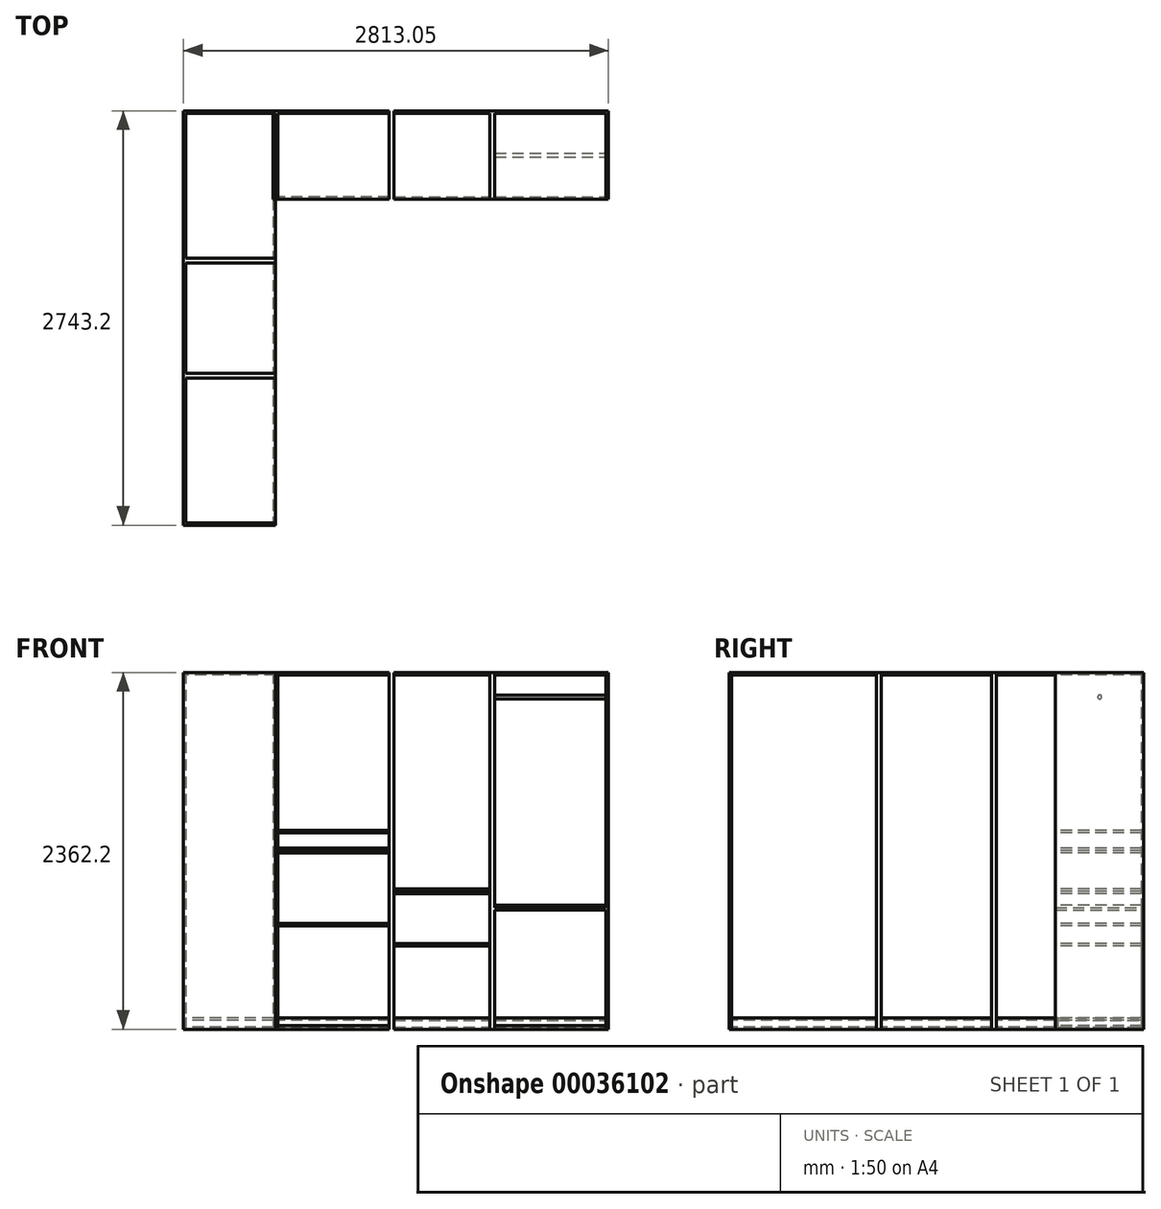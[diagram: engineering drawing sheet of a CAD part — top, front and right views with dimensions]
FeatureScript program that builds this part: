
annotation { "Feature Type Name" : "Feature", "Feature Type Description" : "" }
export const myFeature = defineFeature(function(context is Context, id is Id, definition is map)
    precondition{}
    {
        {
            var Q0;
            Q0=qCreatedBy(makeId("Top.planeOp"),FACE);
            var sketch = newSketch(context, id + "F0", { "sketchPlane" : qUnion([Q0])});
            skLineSegment(sketch, "E0.rect.bottom", {"start": v(384.18, 292.1) * mm, "end": v(-384.18, 292.1) * mm});
            skLineSegment(sketch, "E0.rect.top", {"start": v(384.18, -292.1) * mm, "end": v(-384.18, -292.1) * mm});
            skLineSegment(sketch, "E0.rect.left", {"start": v(384.18, 292.1) * mm, "end": v(384.18, -292.1) * mm});
            skLineSegment(sketch, "E0.rect.right", {"start": v(-384.18, 292.1) * mm, "end": v(-384.18, -292.1) * mm});
            skPoint(sketch, "E0.rect.middle", {"position": v(0, 0) * mm});
            skLineSegment(sketch, "E1.bottom", {"start": v(384.18, -292.1) * mm, "end": v(1050.93, -292.1) * mm});
            skLineSegment(sketch, "E1.top", {"start": v(384.17, 292.1) * mm, "end": v(1050.92, 292.1) * mm});
            skLineSegment(sketch, "E1.left", {"start": v(384.18, -292.1) * mm, "end": v(384.18, 292.1) * mm});
            skLineSegment(sketch, "E1.right", {"start": v(1050.93, -292.1) * mm, "end": v(1050.92, 292.1) * mm});
            skLineSegment(sketch, "E2.bottom", {"start": v(1050.93, -292.1) * mm, "end": v(1819.27, -292.1) * mm});
            skLineSegment(sketch, "E2.top", {"start": v(1050.92, 292.1) * mm, "end": v(1819.27, 292.1) * mm});
            skLineSegment(sketch, "E2.left", {"start": v(1050.93, -292.1) * mm, "end": v(1050.93, 292.1) * mm});
            skLineSegment(sketch, "E2.right", {"start": v(1819.27, -292.1) * mm, "end": v(1819.27, 292.1) * mm});
            skLineSegment(sketch, "E3.bottom", {"start": v(-384.18, 292.1) * mm, "end": v(-993.78, 292.1) * mm});
            skLineSegment(sketch, "E3.top", {"start": v(-384.17, -2451.1) * mm, "end": v(-993.77, -2451.1) * mm});
            skLineSegment(sketch, "E3.left", {"start": v(-384.18, 292.1) * mm, "end": v(-384.18, -2451.1) * mm});
            skLineSegment(sketch, "E3.right", {"start": v(-993.78, 292.1) * mm, "end": v(-993.77, -2451.1) * mm});
            skLineSegment(sketch, "E4.0", {"start": v(1066.8, -276.22) * mm, "end": v(1066.8, 276.22) * mm});
            skLineSegment(sketch, "E4.1", {"start": v(1066.8, -276.22) * mm, "end": v(1803.4, -276.22) * mm});
            skLineSegment(sketch, "E4.2", {"start": v(1803.4, -276.22) * mm, "end": v(1803.4, 276.22) * mm});
            skLineSegment(sketch, "E4.3", {"start": v(1066.8, 276.22) * mm, "end": v(1803.4, 276.22) * mm});
            skLineSegment(sketch, "E5.0", {"start": v(400.05, -276.23) * mm, "end": v(1035.05, -276.23) * mm});
            skLineSegment(sketch, "E5.1", {"start": v(400.05, -276.23) * mm, "end": v(400.05, 276.23) * mm});
            skLineSegment(sketch, "E5.2", {"start": v(400.05, 276.23) * mm, "end": v(1035.05, 276.23) * mm});
            skLineSegment(sketch, "E5.3", {"start": v(1035.05, -276.23) * mm, "end": v(1035.05, 276.23) * mm});
            skLineSegment(sketch, "E6.0", {"start": v(368.3, -276.23) * mm, "end": v(-368.3, -276.23) * mm});
            skLineSegment(sketch, "E6.1", {"start": v(368.3, -276.23) * mm, "end": v(368.3, 276.22) * mm});
            skLineSegment(sketch, "E6.2", {"start": v(368.3, 276.22) * mm, "end": v(-368.3, 276.22) * mm});
            skLineSegment(sketch, "E6.3", {"start": v(-368.3, 276.22) * mm, "end": v(-368.3, -276.23) * mm});
            skLineSegment(sketch, "E7.0", {"start": v(-400.05, 276.22) * mm, "end": v(-977.9, 276.22) * mm});
            skLineSegment(sketch, "E7.1", {"start": v(-400.05, 276.22) * mm, "end": v(-400.05, -682.63) * mm});
            skLineSegment(sketch, "E7.2", {"start": v(-400.05, -2435.23) * mm, "end": v(-977.9, -2435.23) * mm});
            skLineSegment(sketch, "E7.3", {"start": v(-977.9, 276.22) * mm, "end": v(-977.9, -682.63) * mm});
            skLineSegment(sketch, "E8", {"start": v(-368.3, 276.22) * mm, "end": v(-368.3, 292.1) * mm});
            skLineSegment(sketch, "E9", {"start": v(-368.3, -276.23) * mm, "end": v(-368.3, -292.1) * mm});
            skLineSegment(sketch, "E10", {"start": v(-400.05, 276.22) * mm, "end": v(-384.18, 276.22) * mm});
            skLineSegment(sketch, "E11", {"start": v(368.3, -276.23) * mm, "end": v(368.3, -292.1) * mm});
            skLineSegment(sketch, "E12", {"start": v(368.3, 276.22) * mm, "end": v(368.3, 292.1) * mm});
            skLineSegment(sketch, "E13", {"start": v(400.05, -276.23) * mm, "end": v(400.05, -292.1) * mm});
            skLineSegment(sketch, "E14", {"start": v(400.05, 276.23) * mm, "end": v(400.05, 292.1) * mm});
            skLineSegment(sketch, "E15", {"start": v(1035.05, 276.23) * mm, "end": v(1035.05, 292.1) * mm});
            skLineSegment(sketch, "E16", {"start": v(1066.8, 276.22) * mm, "end": v(1066.8, 292.1) * mm});
            skLineSegment(sketch, "E17", {"start": v(1035.05, -276.23) * mm, "end": v(1035.05, -292.1) * mm});
            skLineSegment(sketch, "E18", {"start": v(1066.8, -276.22) * mm, "end": v(1066.8, -292.1) * mm});
            skLineSegment(sketch, "E19", {"start": v(1803.4, 276.22) * mm, "end": v(1803.4, 292.1) * mm});
            skLineSegment(sketch, "E20", {"start": v(1803.4, -276.22) * mm, "end": v(1803.4, -292.1) * mm});
            skLineSegment(sketch, "E21", {"start": v(-977.9, 276.22) * mm, "end": v(-993.78, 276.22) * mm});
            skLineSegment(sketch, "E22.0", {"start": v(-384.18, -698.5) * mm, "end": v(-993.77, -698.5) * mm});
            skLineSegment(sketch, "E23", {"start": v(-977.9, -2435.23) * mm, "end": v(-993.77, -2435.23) * mm});
            skLineSegment(sketch, "E24", {"start": v(-400.05, -2435.23) * mm, "end": v(-384.18, -2435.23) * mm});
            skLineSegment(sketch, "E25.0", {"start": v(-384.17, -1460.5) * mm, "end": v(-993.77, -1460.5) * mm});
            skLineSegment(sketch, "E26.0", {"start": v(-384.18, -714.38) * mm, "end": v(-993.77, -714.38) * mm});
            skLineSegment(sketch, "E27.0", {"start": v(-384.18, -682.63) * mm, "end": v(-993.77, -682.63) * mm});
            skLineSegment(sketch, "E28.0", {"start": v(-384.17, -1444.62) * mm, "end": v(-993.77, -1444.62) * mm});
            skLineSegment(sketch, "E29.0", {"start": v(-384.17, -1476.38) * mm, "end": v(-993.77, -1476.38) * mm});
            skLineSegment(sketch, "E30.trimOffspring", {"start": v(-977.9, -714.38) * mm, "end": v(-977.9, -1444.62) * mm});
            skLineSegment(sketch, "E31.trimOffspring", {"start": v(-400.05, -714.38) * mm, "end": v(-400.05, -1444.62) * mm});
            skLineSegment(sketch, "E32.trimOffspring", {"start": v(-977.9, -1476.38) * mm, "end": v(-977.9, -2435.23) * mm});
            skLineSegment(sketch, "E33.trimOffspring", {"start": v(-400.05, -1476.38) * mm, "end": v(-400.05, -2435.23) * mm});
            skLineSegment(sketch, "E34", {"start": v(-384.18, -292.1) * mm, "end": v(-400.05, -292.1) * mm});
            skLineSegment(sketch, "E35.bottom", {"start": v(-384.17, -2451.1) * mm, "end": v(384.18, -2451.1) * mm});
            skLineSegment(sketch, "E35.top", {"start": v(-384.17, -1866.9) * mm, "end": v(384.18, -1866.9) * mm});
            skLineSegment(sketch, "E35.left", {"start": v(-384.17, -2451.1) * mm, "end": v(-384.17, -1866.9) * mm});
            skLineSegment(sketch, "E35.right", {"start": v(384.18, -2451.1) * mm, "end": v(384.18, -1866.9) * mm});
            skLineSegment(sketch, "E36", {"start": v(-384.17, -1866.9) * mm, "end": v(-400.05, -1866.9) * mm});
            skSolve(sketch);
        }
        {
            var Q0;
            {var subQ2=sQuery(id+"F0.wireOp",EDGE,"E30.trimOffspring");Q0=makeQuery(id+"F0.imprint","IMPRINT",FACE,{"disambiguationData":[TD([[makeQuery(id+"F0.imprint","IMPRINT",EDGE,{"derivedFrom":subQ2}),1.0]])]});}
            var Q1;
            Q1=makeQuery(id+"F0.imprint","IMPRINT",FACE,{"disambiguationData":[TD([[makeQuery(id+"F0.imprint","IMPRINT",EDGE,{"derivedFrom":sQuery(id+"F0.wireOp",EDGE,"E7.2")}),-1.0]])]});
            var Q2;
            {var subQ5=sQuery(id+"F0.wireOp",EDGE,"E7.0");Q2=makeQuery(id+"F0.imprint","IMPRINT",FACE,{"disambiguationData":[TD([[makeQuery(id+"F0.imprint","IMPRINT",EDGE,{"derivedFrom":subQ5}),1.0]])]});}
            var Q3;
            Q3=makeQuery(id+"F0.imprint","IMPRINT",FACE,{"disambiguationData":[TD([[makeQuery(id+"F0.imprint","IMPRINT",EDGE,{"derivedFrom":sQuery(id+"F0.wireOp",EDGE,"E6.0")}),-1.0]])]});
            var Q4;
            Q4=makeQuery(id+"F0.imprint","IMPRINT",FACE,{"disambiguationData":[TD([[makeQuery(id+"F0.imprint","IMPRINT",EDGE,{"derivedFrom":sQuery(id+"F0.wireOp",EDGE,"E5.0")}),1.0]])]});
            var Q5;
            Q5=makeQuery(id+"F0.imprint","IMPRINT",FACE,{"disambiguationData":[TD([[makeQuery(id+"F0.imprint","IMPRINT",EDGE,{"derivedFrom":sQuery(id+"F0.wireOp",EDGE,"E4.0")}),-1.0]])]});
            extrude(context, id + "F1", {"entities" : qUnion([Q0, Q1, Q2, Q3, Q4, Q5]), "depth" : 15.88 * mm});
        }
        {
            var Q0;
            {var subQ3=sQuery(id+"F0.wireOp",EDGE,"E3.top");Q0=makeQuery(id+"F0.imprint","IMPRINT",FACE,{"disambiguationData":[TD([[makeQuery(id+"F0.imprint","IMPRINT",EDGE,{"derivedFrom":subQ3}),-1.0]])]});}
            var Q1;
            {var subQ4=sQuery(id+"F0.wireOp",EDGE,"E23");Q1=makeQuery(id+"F0.imprint","IMPRINT",FACE,{"disambiguationData":[TD([[makeQuery(id+"F0.imprint","IMPRINT",EDGE,{"derivedFrom":subQ4}),-1.0]])]});}
            var Q2;
            {var subQ7=sQuery(id+"F0.wireOp",EDGE,"E25.0");Q2=makeQuery(id+"F0.imprint","IMPRINT",FACE,{"disambiguationData":[TD([[makeQuery(id+"F0.imprint","IMPRINT",EDGE,{"derivedFrom":subQ7}),1.0]])]});}
            var Q3;
            {var subQ7=sQuery(id+"F0.wireOp",EDGE,"E25.0");Q3=makeQuery(id+"F0.imprint","IMPRINT",FACE,{"disambiguationData":[TD([[makeQuery(id+"F0.imprint","IMPRINT",EDGE,{"derivedFrom":subQ7}),-1.0]])]});}
            var Q4;
            {var subQ1=sQuery(id+"F0.wireOp",EDGE,"E30.trimOffspring");Q4=makeQuery(id+"F0.imprint","IMPRINT",FACE,{"disambiguationData":[TD([[makeQuery(id+"F0.imprint","IMPRINT",EDGE,{"derivedFrom":subQ1}),-1.0]])]});}
            var Q5;
            {var subQ5=sQuery(id+"F0.wireOp",EDGE,"E22.0");Q5=makeQuery(id+"F0.imprint","IMPRINT",FACE,{"disambiguationData":[TD([[makeQuery(id+"F0.imprint","IMPRINT",EDGE,{"derivedFrom":subQ5}),1.0]])]});}
            var Q6;
            {var subQ7=sQuery(id+"F0.wireOp",EDGE,"E22.0");Q6=makeQuery(id+"F0.imprint","IMPRINT",FACE,{"disambiguationData":[TD([[makeQuery(id+"F0.imprint","IMPRINT",EDGE,{"derivedFrom":subQ7}),-1.0]])]});}
            var Q7;
            {var subQ1=sQuery(id+"F0.wireOp",EDGE,"E10");Q7=makeQuery(id+"F0.imprint","IMPRINT",FACE,{"disambiguationData":[TD([[makeQuery(id+"F0.imprint","IMPRINT",EDGE,{"derivedFrom":subQ1}),-1.0]])]});}
            var Q8;
            Q8=makeQuery(id+"F0.imprint","IMPRINT",FACE,{"disambiguationData":[TD([[makeQuery(id+"F0.imprint","IMPRINT",EDGE,{"derivedFrom":sQuery(id+"F0.wireOp",EDGE,"E6.3")}),-1.0]])]});
            var Q9;
            {var subQ3=sQuery(id+"F0.wireOp",EDGE,"E7.3");Q9=makeQuery(id+"F0.imprint","IMPRINT",FACE,{"disambiguationData":[TD([[makeQuery(id+"F0.imprint","IMPRINT",EDGE,{"derivedFrom":subQ3}),-1.0]])]});}
            var Q10;
            {var subQ3=sQuery(id+"F0.wireOp",EDGE,"E3.bottom");Q10=makeQuery(id+"F0.imprint","IMPRINT",FACE,{"disambiguationData":[TD([[makeQuery(id+"F0.imprint","IMPRINT",EDGE,{"derivedFrom":subQ3}),1.0]])]});}
            var Q11;
            Q11=makeQuery(id+"F0.imprint","IMPRINT",FACE,{"disambiguationData":[TD([[makeQuery(id+"F0.imprint","IMPRINT",EDGE,{"derivedFrom":sQuery(id+"F0.wireOp",EDGE,"E6.2")}),-1.0]])]});
            var Q12;
            {var subQ2=sQuery(id+"F0.wireOp",EDGE,"E1.left");Q12=makeQuery(id+"F0.imprint","IMPRINT",FACE,{"disambiguationData":[TD([[makeQuery(id+"F0.imprint","IMPRINT",EDGE,{"derivedFrom":subQ2}),1.0]])]});}
            var Q13;
            {var subQ1=sQuery(id+"F0.wireOp",EDGE,"E1.left");Q13=makeQuery(id+"F0.imprint","IMPRINT",FACE,{"disambiguationData":[TD([[makeQuery(id+"F0.imprint","IMPRINT",EDGE,{"derivedFrom":subQ1}),-1.0]])]});}
            var Q14;
            Q14=makeQuery(id+"F0.imprint","IMPRINT",FACE,{"disambiguationData":[TD([[makeQuery(id+"F0.imprint","IMPRINT",EDGE,{"derivedFrom":sQuery(id+"F0.wireOp",EDGE,"E5.2")}),1.0]])]});
            var Q15;
            {var subQ1=sQuery(id+"F0.wireOp",EDGE,"E2.left");Q15=makeQuery(id+"F0.imprint","IMPRINT",FACE,{"disambiguationData":[TD([[makeQuery(id+"F0.imprint","IMPRINT",EDGE,{"derivedFrom":subQ1}),1.0]])]});}
            var Q16;
            {var subQ2=sQuery(id+"F0.wireOp",EDGE,"E2.left");Q16=makeQuery(id+"F0.imprint","IMPRINT",FACE,{"disambiguationData":[TD([[makeQuery(id+"F0.imprint","IMPRINT",EDGE,{"derivedFrom":subQ2}),-1.0]])]});}
            var Q17;
            Q17=makeQuery(id+"F0.imprint","IMPRINT",FACE,{"disambiguationData":[TD([[makeQuery(id+"F0.imprint","IMPRINT",EDGE,{"derivedFrom":sQuery(id+"F0.wireOp",EDGE,"E4.3")}),1.0]])]});
            var Q18;
            {var subQ2=sQuery(id+"F0.wireOp",EDGE,"E2.right");Q18=makeQuery(id+"F0.imprint","IMPRINT",FACE,{"disambiguationData":[TD([[makeQuery(id+"F0.imprint","IMPRINT",EDGE,{"derivedFrom":subQ2}),1.0]])]});}
            extrude(context, id + "F2", {"entities" : qUnion([Q0, Q1, Q2, Q3, Q4, Q5, Q6, Q7, Q8, Q9, Q10, Q11, Q12, Q13, Q14, Q15, Q16, Q17, Q18]), "depth" : 2362.2 * mm});
        }
        {
            var Q0;
            {var subQ2=sQuery(id+"F0.wireOp",EDGE,"E24");Q0=makeQuery(id+"F0.imprint","IMPRINT",FACE,{"disambiguationData":[TD([[makeQuery(id+"F0.imprint","IMPRINT",EDGE,{"derivedFrom":subQ2}),1.0]])]});}
            var Q1;
            {var subQ0=sQuery(id+"F0.wireOp",EDGE,"E36");Q1=makeQuery(id+"F0.imprint","IMPRINT",FACE,{"disambiguationData":[TD([[makeQuery(id+"F0.imprint","IMPRINT",EDGE,{"derivedFrom":subQ0}),-1.0]])]});}
            var Q2;
            {var subQ0=sQuery(id+"F0.wireOp",EDGE,"E31.trimOffspring");Q2=makeQuery(id+"F0.imprint","IMPRINT",FACE,{"disambiguationData":[TD([[makeQuery(id+"F0.imprint","IMPRINT",EDGE,{"derivedFrom":subQ0}),1.0]])]});}
            var Q3;
            {var subQ0=sQuery(id+"F0.wireOp",EDGE,"E34");Q3=makeQuery(id+"F0.imprint","IMPRINT",FACE,{"disambiguationData":[TD([[makeQuery(id+"F0.imprint","IMPRINT",EDGE,{"derivedFrom":subQ0}),1.0]])]});}
            var Q4;
            Q4=makeQuery(id+"F0.imprint","IMPRINT",FACE,{"disambiguationData":[TD([[makeQuery(id+"F0.imprint","IMPRINT",EDGE,{"derivedFrom":sQuery(id+"F0.wireOp",EDGE,"E6.0")}),1.0]])]});
            var Q5;
            Q5=makeQuery(id+"F0.imprint","IMPRINT",FACE,{"disambiguationData":[TD([[makeQuery(id+"F0.imprint","IMPRINT",EDGE,{"derivedFrom":sQuery(id+"F0.wireOp",EDGE,"E5.0")}),-1.0]])]});
            var Q6;
            Q6=makeQuery(id+"F0.imprint","IMPRINT",FACE,{"disambiguationData":[TD([[makeQuery(id+"F0.imprint","IMPRINT",EDGE,{"derivedFrom":sQuery(id+"F0.wireOp",EDGE,"E4.1")}),-1.0]])]});
            extrude(context, id + "F3", {"entities" : qUnion([Q0, Q1, Q2, Q3, Q4, Q5, Q6]), "depth" : 76.2 * mm});
        }
        {
            var Q0;
            {var subQ2=sQuery(id+"F0.wireOp",EDGE,"E7.2");Q0=makeQuery(id+"F0.imprint","IMPRINT",FACE,{"disambiguationData":[TD([[makeQuery(id+"F0.imprint","IMPRINT",EDGE,{"derivedFrom":subQ2}),-1.0]])]});}
            var Q1;
            {var subQ2=sQuery(id+"F0.wireOp",EDGE,"E30.trimOffspring");Q1=makeQuery(id+"F0.imprint","IMPRINT",FACE,{"disambiguationData":[TD([[makeQuery(id+"F0.imprint","IMPRINT",EDGE,{"derivedFrom":subQ2}),1.0]])]});}
            var Q2;
            {var subQ5=sQuery(id+"F0.wireOp",EDGE,"E7.0");Q2=makeQuery(id+"F0.imprint","IMPRINT",FACE,{"disambiguationData":[TD([[makeQuery(id+"F0.imprint","IMPRINT",EDGE,{"derivedFrom":subQ5}),1.0]])]});}
            var Q3;
            Q3=makeQuery(id+"F0.imprint","IMPRINT",FACE,{"disambiguationData":[TD([[makeQuery(id+"F0.imprint","IMPRINT",EDGE,{"derivedFrom":sQuery(id+"F0.wireOp",EDGE,"E6.0")}),-1.0]])]});
            var Q4;
            Q4=makeQuery(id+"F0.imprint","IMPRINT",FACE,{"disambiguationData":[TD([[makeQuery(id+"F0.imprint","IMPRINT",EDGE,{"derivedFrom":sQuery(id+"F0.wireOp",EDGE,"E5.0")}),1.0]])]});
            var Q5;
            Q5=makeQuery(id+"F0.imprint","IMPRINT",FACE,{"disambiguationData":[TD([[makeQuery(id+"F0.imprint","IMPRINT",EDGE,{"derivedFrom":sQuery(id+"F0.wireOp",EDGE,"E4.0")}),-1.0]])]});
            extrude(context, id + "F4", {"entities" : qUnion([Q0, Q1, Q2, Q3, Q4, Q5]), "depth" : 76.2 * mm, "hasSecondDirection" : true, "secondDirectionOppositeDirection" : false, "secondDirectionDepth" : 60.32 * mm});
        }
        {
            var Q0;
            {var subQ2=sQuery(id+"F0.wireOp",EDGE,"E24");Q0=makeQuery(id+"F0.imprint","IMPRINT",FACE,{"disambiguationData":[TD([[makeQuery(id+"F0.imprint","IMPRINT",EDGE,{"derivedFrom":subQ2}),1.0]])]});}
            var Q1;
            {var subQ0=sQuery(id+"F0.wireOp",EDGE,"E36");Q1=makeQuery(id+"F0.imprint","IMPRINT",FACE,{"disambiguationData":[TD([[makeQuery(id+"F0.imprint","IMPRINT",EDGE,{"derivedFrom":subQ0}),-1.0]])]});}
            var Q2;
            {var subQ2=sQuery(id+"F0.wireOp",EDGE,"E7.2");Q2=makeQuery(id+"F0.imprint","IMPRINT",FACE,{"disambiguationData":[TD([[makeQuery(id+"F0.imprint","IMPRINT",EDGE,{"derivedFrom":subQ2}),-1.0]])]});}
            var Q3;
            {var subQ0=sQuery(id+"F0.wireOp",EDGE,"E31.trimOffspring");Q3=makeQuery(id+"F0.imprint","IMPRINT",FACE,{"disambiguationData":[TD([[makeQuery(id+"F0.imprint","IMPRINT",EDGE,{"derivedFrom":subQ0}),1.0]])]});}
            var Q4;
            {var subQ2=sQuery(id+"F0.wireOp",EDGE,"E30.trimOffspring");Q4=makeQuery(id+"F0.imprint","IMPRINT",FACE,{"disambiguationData":[TD([[makeQuery(id+"F0.imprint","IMPRINT",EDGE,{"derivedFrom":subQ2}),1.0]])]});}
            var Q5;
            {var subQ1=sQuery(id+"F0.wireOp",EDGE,"E10");Q5=makeQuery(id+"F0.imprint","IMPRINT",FACE,{"disambiguationData":[TD([[makeQuery(id+"F0.imprint","IMPRINT",EDGE,{"derivedFrom":subQ1}),-1.0]])]});}
            var Q6;
            {var subQ0=sQuery(id+"F0.wireOp",EDGE,"E34");Q6=makeQuery(id+"F0.imprint","IMPRINT",FACE,{"disambiguationData":[TD([[makeQuery(id+"F0.imprint","IMPRINT",EDGE,{"derivedFrom":subQ0}),1.0]])]});}
            var Q7;
            {var subQ5=sQuery(id+"F0.wireOp",EDGE,"E7.0");Q7=makeQuery(id+"F0.imprint","IMPRINT",FACE,{"disambiguationData":[TD([[makeQuery(id+"F0.imprint","IMPRINT",EDGE,{"derivedFrom":subQ5}),1.0]])]});}
            var Q8;
            Q8=makeQuery(id+"F0.imprint","IMPRINT",FACE,{"disambiguationData":[TD([[makeQuery(id+"F0.imprint","IMPRINT",EDGE,{"derivedFrom":sQuery(id+"F0.wireOp",EDGE,"E6.0")}),1.0]])]});
            var Q9;
            Q9=makeQuery(id+"F0.imprint","IMPRINT",FACE,{"disambiguationData":[TD([[makeQuery(id+"F0.imprint","IMPRINT",EDGE,{"derivedFrom":sQuery(id+"F0.wireOp",EDGE,"E6.0")}),-1.0]])]});
            var Q10;
            Q10=makeQuery(id+"F0.imprint","IMPRINT",FACE,{"disambiguationData":[TD([[makeQuery(id+"F0.imprint","IMPRINT",EDGE,{"derivedFrom":sQuery(id+"F0.wireOp",EDGE,"E5.0")}),-1.0]])]});
            var Q11;
            Q11=makeQuery(id+"F0.imprint","IMPRINT",FACE,{"disambiguationData":[TD([[makeQuery(id+"F0.imprint","IMPRINT",EDGE,{"derivedFrom":sQuery(id+"F0.wireOp",EDGE,"E5.0")}),1.0]])]});
            var Q12;
            Q12=makeQuery(id+"F0.imprint","IMPRINT",FACE,{"disambiguationData":[TD([[makeQuery(id+"F0.imprint","IMPRINT",EDGE,{"derivedFrom":sQuery(id+"F0.wireOp",EDGE,"E4.1")}),-1.0]])]});
            var Q13;
            Q13=makeQuery(id+"F0.imprint","IMPRINT",FACE,{"disambiguationData":[TD([[makeQuery(id+"F0.imprint","IMPRINT",EDGE,{"derivedFrom":sQuery(id+"F0.wireOp",EDGE,"E4.0")}),-1.0]])]});
            extrude(context, id + "F5", {"entities" : qUnion([Q0, Q1, Q2, Q3, Q4, Q5, Q6, Q7, Q8, Q9, Q10, Q11, Q12, Q13]), "depth" : 2362.2 * mm, "hasSecondDirection" : true, "secondDirectionOppositeDirection" : false, "secondDirectionDepth" : 2346.32 * mm});
        }
        {
            var Q0;
            Q0=makeQuery(id+"F0.imprint","IMPRINT",FACE,{"disambiguationData":[TD([[makeQuery(id+"F0.imprint","IMPRINT",EDGE,{"derivedFrom":sQuery(id+"F0.wireOp",EDGE,"E6.0")}),1.0]])]});
            var Q1;
            Q1=makeQuery(id+"F0.imprint","IMPRINT",FACE,{"disambiguationData":[TD([[makeQuery(id+"F0.imprint","IMPRINT",EDGE,{"derivedFrom":sQuery(id+"F0.wireOp",EDGE,"E6.0")}),-1.0]])]});
            extrude(context, id + "F6", {"entities" : qUnion([Q0, Q1]), "depth" : 25.4 * mm});
        }
        {
            var Q0;
            Q0=makeQuery(id+"F0.imprint","IMPRINT",FACE,{"disambiguationData":[TD([[makeQuery(id+"F0.imprint","IMPRINT",EDGE,{"derivedFrom":sQuery(id+"F0.wireOp",EDGE,"E6.0")}),-1.0]])]});
            var Q1;
            Q1=makeQuery(id+"F0.imprint","IMPRINT",FACE,{"disambiguationData":[TD([[makeQuery(id+"F0.imprint","IMPRINT",EDGE,{"derivedFrom":sQuery(id+"F0.wireOp",EDGE,"E6.0")}),1.0]])]});
            extrude(context, id + "F7", {"entities" : qUnion([Q0, Q1]), "depth" : 701.67 * mm, "hasSecondDirection" : true, "secondDirectionOppositeDirection" : false, "secondDirectionDepth" : 685.8 * mm});
        }
        {
            var Q0;
            Q0=makeQuery(id+"F0.imprint","IMPRINT",FACE,{"disambiguationData":[TD([[makeQuery(id+"F0.imprint","IMPRINT",EDGE,{"derivedFrom":sQuery(id+"F0.wireOp",EDGE,"E6.0")}),1.0]])]});
            var Q1;
            Q1=makeQuery(id+"F0.imprint","IMPRINT",FACE,{"disambiguationData":[TD([[makeQuery(id+"F0.imprint","IMPRINT",EDGE,{"derivedFrom":sQuery(id+"F0.wireOp",EDGE,"E6.0")}),-1.0]])]});
            extrude(context, id + "F8", {"entities" : qUnion([Q0, Q1]), "depth" : 1184.27 * mm, "hasSecondDirection" : true, "secondDirectionOppositeDirection" : false, "secondDirectionDepth" : 1168.4 * mm});
        }
        {
            var Q0;
            Q0=makeQuery(id+"F0.imprint","IMPRINT",FACE,{"disambiguationData":[TD([[makeQuery(id+"F0.imprint","IMPRINT",EDGE,{"derivedFrom":sQuery(id+"F0.wireOp",EDGE,"E6.0")}),1.0]])]});
            var Q1;
            Q1=makeQuery(id+"F0.imprint","IMPRINT",FACE,{"disambiguationData":[TD([[makeQuery(id+"F0.imprint","IMPRINT",EDGE,{"derivedFrom":sQuery(id+"F0.wireOp",EDGE,"E6.0")}),-1.0]])]});
            extrude(context, id + "F9", {"entities" : qUnion([Q0, Q1]), "depth" : 1200.15 * mm, "hasSecondDirection" : true, "secondDirectionOppositeDirection" : false, "secondDirectionDepth" : 1184.27 * mm});
        }
        {
            var Q0;
            Q0=makeQuery(id+"F0.imprint","IMPRINT",FACE,{"disambiguationData":[TD([[makeQuery(id+"F0.imprint","IMPRINT",EDGE,{"derivedFrom":sQuery(id+"F0.wireOp",EDGE,"E6.0")}),-1.0]])]});
            var Q1;
            Q1=makeQuery(id+"F0.imprint","IMPRINT",FACE,{"disambiguationData":[TD([[makeQuery(id+"F0.imprint","IMPRINT",EDGE,{"derivedFrom":sQuery(id+"F0.wireOp",EDGE,"E6.0")}),1.0]])]});
            extrude(context, id + "F10", {"entities" : qUnion([Q0, Q1]), "depth" : 1317.62 * mm, "hasSecondDirection" : true, "secondDirectionOppositeDirection" : false, "secondDirectionDepth" : 1301.75 * mm});
        }
        {
            var Q0;
            Q0=makeQuery(id+"F0.imprint","IMPRINT",FACE,{"disambiguationData":[TD([[makeQuery(id+"F0.imprint","IMPRINT",EDGE,{"derivedFrom":sQuery(id+"F0.wireOp",EDGE,"E5.0")}),-1.0]])]});
            var Q1;
            Q1=makeQuery(id+"F0.imprint","IMPRINT",FACE,{"disambiguationData":[TD([[makeQuery(id+"F0.imprint","IMPRINT",EDGE,{"derivedFrom":sQuery(id+"F0.wireOp",EDGE,"E5.0")}),1.0]])]});
            extrude(context, id + "F11", {"entities" : qUnion([Q0, Q1]), "depth" : 568.32 * mm, "hasSecondDirection" : true, "secondDirectionOppositeDirection" : false, "secondDirectionDepth" : 552.45 * mm});
        }
        {
            var Q0;
            Q0=makeQuery(id+"F0.imprint","IMPRINT",FACE,{"disambiguationData":[TD([[makeQuery(id+"F0.imprint","IMPRINT",EDGE,{"derivedFrom":sQuery(id+"F0.wireOp",EDGE,"E5.0")}),-1.0]])]});
            var Q1;
            Q1=makeQuery(id+"F0.imprint","IMPRINT",FACE,{"disambiguationData":[TD([[makeQuery(id+"F0.imprint","IMPRINT",EDGE,{"derivedFrom":sQuery(id+"F0.wireOp",EDGE,"E5.0")}),1.0]])]});
            extrude(context, id + "F12", {"entities" : qUnion([Q0, Q1]), "depth" : 914.4 * mm, "hasSecondDirection" : true, "secondDirectionOppositeDirection" : false, "secondDirectionDepth" : 898.52 * mm});
        }
        {
            var Q0;
            Q0=makeQuery(id+"F0.imprint","IMPRINT",FACE,{"disambiguationData":[TD([[makeQuery(id+"F0.imprint","IMPRINT",EDGE,{"derivedFrom":sQuery(id+"F0.wireOp",EDGE,"E5.0")}),-1.0]])]});
            var Q1;
            Q1=makeQuery(id+"F0.imprint","IMPRINT",FACE,{"disambiguationData":[TD([[makeQuery(id+"F0.imprint","IMPRINT",EDGE,{"derivedFrom":sQuery(id+"F0.wireOp",EDGE,"E5.0")}),1.0]])]});
            extrude(context, id + "F13", {"entities" : qUnion([Q0, Q1]), "depth" : 930.27 * mm, "hasSecondDirection" : true, "secondDirectionOppositeDirection" : false, "secondDirectionDepth" : 914.4 * mm});
        }
        {
            var Q0;
            Q0=makeQuery(id+"F0.imprint","IMPRINT",FACE,{"disambiguationData":[TD([[makeQuery(id+"F0.imprint","IMPRINT",EDGE,{"derivedFrom":sQuery(id+"F0.wireOp",EDGE,"E4.1")}),-1.0]])]});
            var Q1;
            Q1=makeQuery(id+"F0.imprint","IMPRINT",FACE,{"disambiguationData":[TD([[makeQuery(id+"F0.imprint","IMPRINT",EDGE,{"derivedFrom":sQuery(id+"F0.wireOp",EDGE,"E4.0")}),-1.0]])]});
            extrude(context, id + "F14", {"entities" : qUnion([Q0, Q1]), "depth" : 25.4 * mm});
        }
        {
            var Q0;
            Q0=makeQuery(id+"F0.imprint","IMPRINT",FACE,{"disambiguationData":[TD([[makeQuery(id+"F0.imprint","IMPRINT",EDGE,{"derivedFrom":sQuery(id+"F0.wireOp",EDGE,"E4.0")}),-1.0]])]});
            var Q1;
            Q1=makeQuery(id+"F0.imprint","IMPRINT",FACE,{"disambiguationData":[TD([[makeQuery(id+"F0.imprint","IMPRINT",EDGE,{"derivedFrom":sQuery(id+"F0.wireOp",EDGE,"E4.1")}),-1.0]])]});
            extrude(context, id + "F15", {"entities" : qUnion([Q0, Q1]), "operationType" : NewBodyOperationType.ADD, "depth" : 806.45 * mm, "hasSecondDirection" : true, "secondDirectionOppositeDirection" : false, "secondDirectionDepth" : 790.57 * mm});
        }
        {
            var Q0;
            Q0=makeQuery(id+"F0.imprint","IMPRINT",FACE,{"disambiguationData":[TD([[makeQuery(id+"F0.imprint","IMPRINT",EDGE,{"derivedFrom":sQuery(id+"F0.wireOp",EDGE,"E4.1")}),-1.0]])]});
            var Q1;
            Q1=makeQuery(id+"F0.imprint","IMPRINT",FACE,{"disambiguationData":[TD([[makeQuery(id+"F0.imprint","IMPRINT",EDGE,{"derivedFrom":sQuery(id+"F0.wireOp",EDGE,"E4.0")}),-1.0]])]});
            extrude(context, id + "F16", {"entities" : qUnion([Q0, Q1]), "depth" : 822.32 * mm, "hasSecondDirection" : true, "secondDirectionOppositeDirection" : false, "secondDirectionDepth" : 806.45 * mm});
        }
        {
            var Q0;
            Q0=makeQuery(id+"F2.opExtrude","SWEPT_FACE",FACE,{"disambiguationData":[OSD([sQuery(id+"F0.wireOp",EDGE,"E2.right")])]});
            var sketch = newSketch(context, id + "F17", { "sketchPlane" : qUnion([Q0])});
            skPoint(sketch, "E37.center.orphan", {"position": v(0, 2199.68) * mm});
            skCircle(sketch, "E38", {"center": v(0, 2199.68) * mm, "radius": 12.7 * mm});
            skSolve(sketch);
        }
        {
            var Q0;
            Q0 = qSketchRegion(id + "F17", true);
            extrude(context, id + "F18", {"entities" : qUnion([Q0]), "operationType" : NewBodyOperationType.ADD, "oppositeDirection" : true, "depth" : 768.35 * mm});
        }
        {
            var Q0;
            Q0=sQuery(id+"F17.wireOp",EDGE,"E38");
            extrude(context, id + "F19", {"bodyType" : ToolBodyType.SURFACE, "surfaceEntities" : qUnion([Q0]), "oppositeDirection" : true, "depth" : 2203.45 * mm, "hasSecondDirection" : true, "secondDirectionOppositeDirection" : true, "secondDirectionDepth" : 1435.1 * mm});
        }
    });
